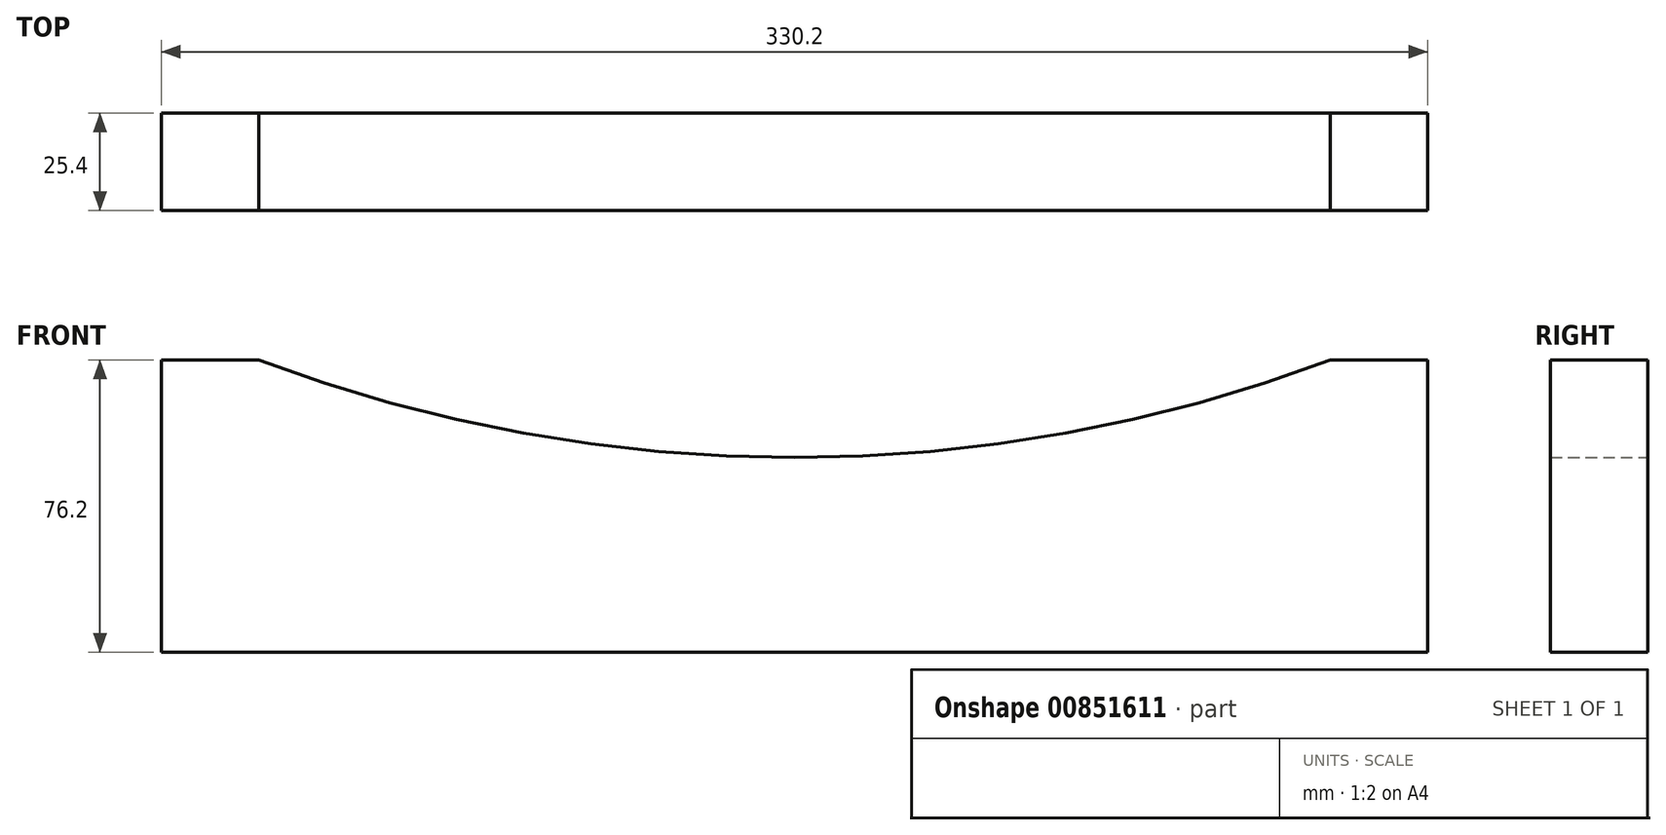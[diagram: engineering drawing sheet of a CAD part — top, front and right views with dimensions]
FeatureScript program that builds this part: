
annotation { "Feature Type Name" : "Feature", "Feature Type Description" : "" }
export const myFeature = defineFeature(function(context is Context, id is Id, definition is map)
    precondition{}
    {
        {
            var Q0;
            Q0=qCreatedBy(makeId("Front.planeOp"),FACE);
            var sketch = newSketch(context, id + "F0", { "sketchPlane" : qUnion([Q0])});
            skLineSegment(sketch, "E0", {"start": v(-55.37, -50.8) * mm, "end": v(274.83, -50.8) * mm});
            skLineSegment(sketch, "E1", {"start": v(274.83, -50.8) * mm, "end": v(274.83, 25.4) * mm});
            skLineSegment(sketch, "E2", {"start": v(-55.37, -50.8) * mm, "end": v(-55.37, 25.4) * mm});
            skLineSegment(sketch, "E3", {"start": v(-55.37, 25.4) * mm, "end": v(-29.97, 25.4) * mm});
            skLineSegment(sketch, "E4", {"start": v(274.83, 25.4) * mm, "end": v(249.43, 25.4) * mm});
            skArc(sketch, "E5", {"start": v(-29.97, 25.4) * mm, "mid": v(109.73, 0) * mm, "end": v(249.43, 25.4) * mm});
            skSolve(sketch);
        }
        {
            var Q0;
            Q0 = qSketchRegion(id + "F0", true);
            extrude(context, id + "F1", {"entities" : qUnion([Q0]), "depth" : 25.4 * mm, "offsetDistance" : 25.4 * mm});
        }
    });
